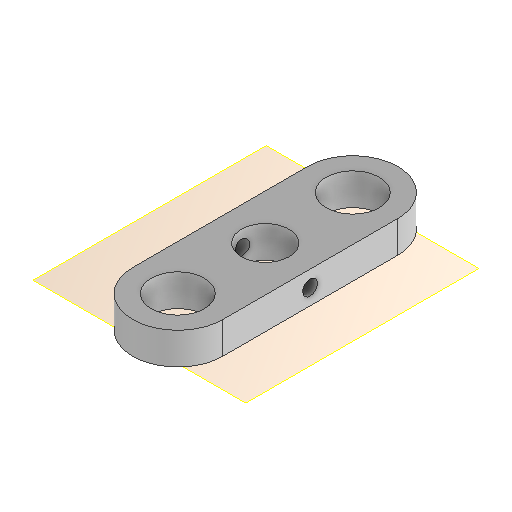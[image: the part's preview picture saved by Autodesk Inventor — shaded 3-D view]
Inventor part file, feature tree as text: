
AUTODESK INVENTOR PART (.ipt)
format: ipt  version: 2024.1 (Build 281209000, 209)  size: 135,168 bytes
history: native  units: mm
features: other x3, extrude x2, sketch x2, plane x1, reference x1
ambient origin geometry x8: Origin, YZ Plane, XZ Plane, XY Plane, X Axis, Y Axis, Z Axis, Center Point
bodies: Volumenkörper1 (feature_tree)
feature tree (9):
  plane  "Arbeitsebene1"
  extrude  "Extrusion1"  Depth=10.0mm
  extrude  "Extrusion2"  Depth=17.0mm
  sketch  "Skizze1"  dims[d0=10.0mm d1=10.0mm]
  reference  "Referenz1"
  sketch  "Skizze2"  dims[d2=9.0mm d3=17.0mm d4=6.0mm d5=0.0mm d6=2.8mm d7=0.0mm d8=0.0mm]
  other  "Application_Investigator_Lighsheet.iam"
  other  "40_XYZstage_micrometer_motorized_nema8_samplemount_lightsheet_screwed:1"
  other  "Baugruppe2"
